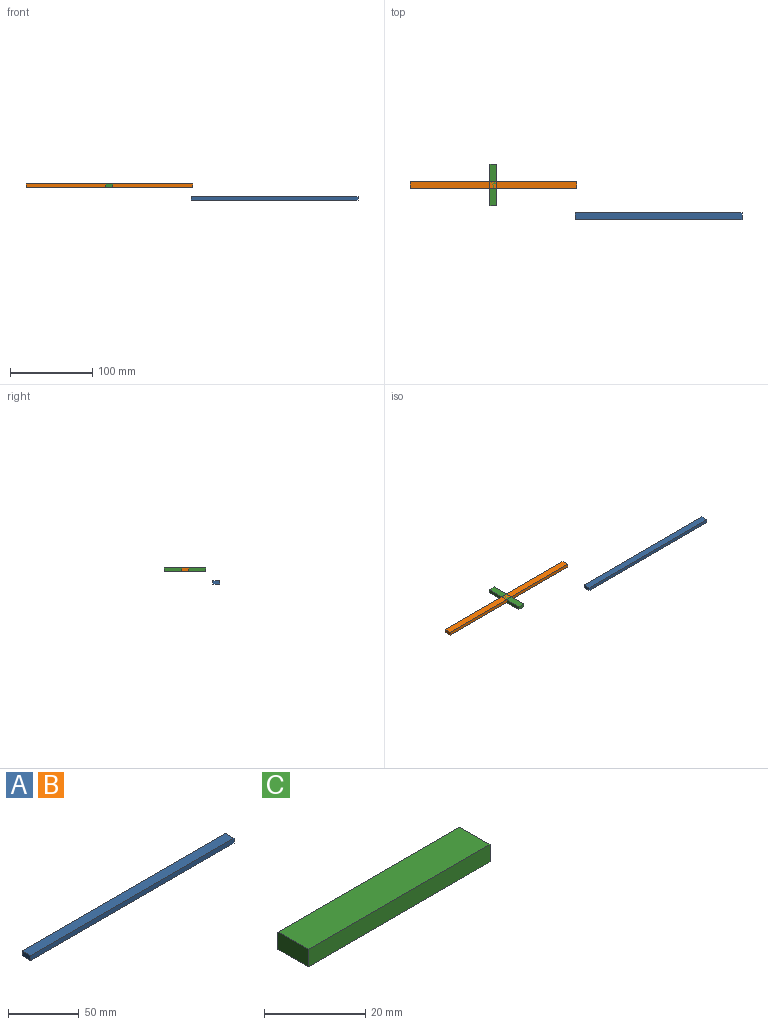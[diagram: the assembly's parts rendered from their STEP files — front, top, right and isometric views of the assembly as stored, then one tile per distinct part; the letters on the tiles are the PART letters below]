
ASSEMBLY  parts=3 mates=4
PART A: 6 faces, bbox 203.2x8.5x4.2 mm
  f0: plane 8.46x4.22mm, normal (-1,0,0), area 35.7mm2, adj f1,f3,f4,f5
  f1: plane 203.2x4.22mm, normal (0,-1,0), area 856.8mm2, adj f0,f2,f4,f5
  f2: plane 8.46x4.22mm, normal (1,0,0), area 35.7mm2, adj f1,f3,f4,f5
  f3: plane 203.2x4.22mm, normal (0,1,0), area 856.8mm2, adj f0,f2,f4,f5
  f4: plane 203.2x8.46mm, normal (0,0,1), area 1718.7mm2, adj f0,f1,f2,f3
  f5: plane 203.2x8.46mm, normal (0,0,-1), area 1718.7mm2, adj f0,f1,f2,f3
PART B: same geometry as A
PART C: 6 faces, bbox 50.8x8.5x4.2 mm
  f0: plane 8.46x4.22mm, normal (-1,0,0), area 35.7mm2, adj f1,f3,f4,f5
  f1: plane 50.8x4.22mm, normal (0,-1,0), area 214.2mm2, adj f0,f2,f4,f5
  f2: plane 8.46x4.22mm, normal (1,0,0), area 35.7mm2, adj f1,f3,f4,f5
  f3: plane 50.8x4.22mm, normal (0,1,0), area 214.2mm2, adj f0,f2,f4,f5
  f4: plane 50.8x8.46mm, normal (0,0,1), area 429.7mm2, adj f0,f1,f2,f3
  f5: plane 50.8x8.46mm, normal (0,0,-1), area 429.7mm2, adj f0,f1,f2,f3
PLACE A t=(-57.38,-14.61,0.91)mm
PLACE B rot(axis=(0,0,1),180deg) t=(-139.28,59.47,16.31)mm
PLACE C rot(axis=(0,0,-1),90deg) t=(-207.24,40.73,16.31)mm
MATE parallel C.f5 <-> B.f5  axis (0,0,-1) through (-199.12,41.42,16.31)mm
MATE parallel C.f0 <-> B.f1  axis (0,1,0) through (-199.12,66.82,18.42)mm
MATE parallel C.f3 <-> B.f0  axis (1,0,0) through (-194.89,66.82,16.31)mm
MATE parallel C.f4 <-> B.f4  axis (0,0,1) through (-199.12,41.42,20.52)mm
